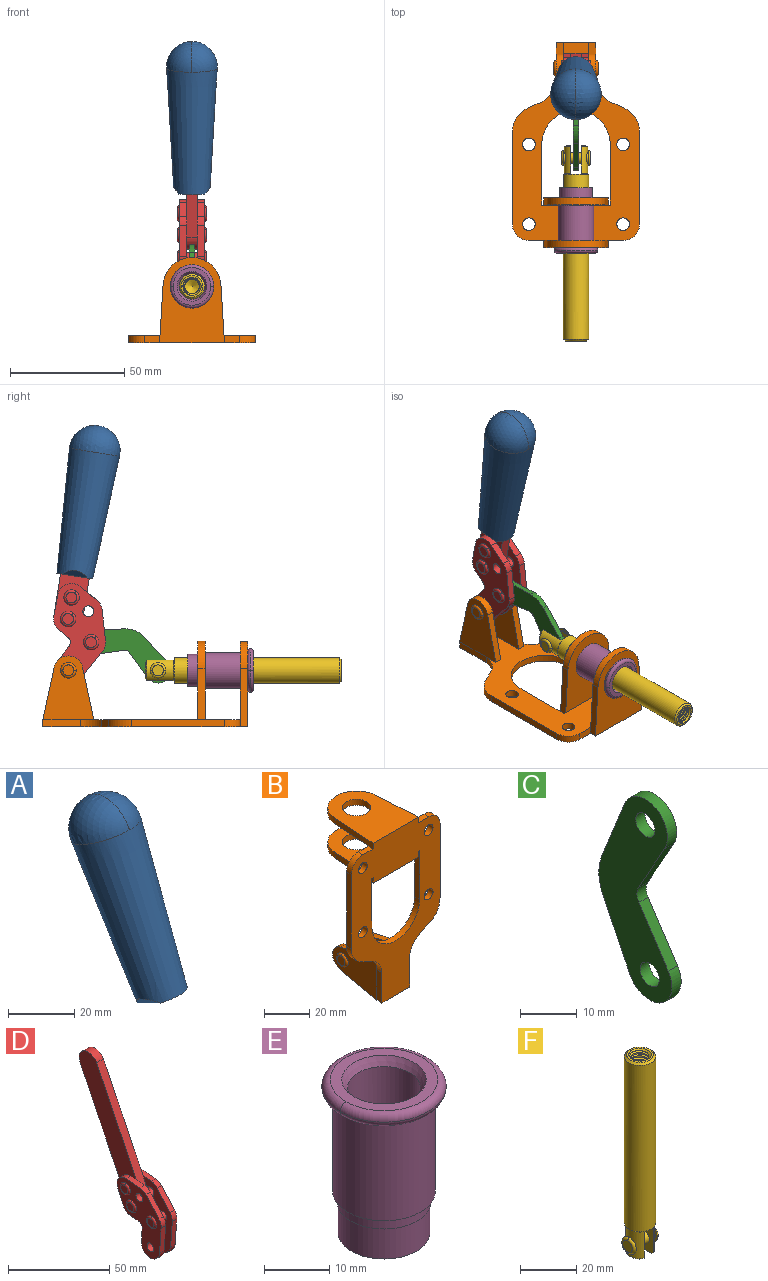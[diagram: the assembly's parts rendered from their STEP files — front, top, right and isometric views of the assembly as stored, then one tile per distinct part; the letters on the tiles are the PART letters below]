
ASSEMBLY  parts=6 mates=6
PART A: 11 faces, bbox 22.3x42.6x64.5 mm
  f0: sphere r=11.13mm, area 411.4mm2, adj f1,f8
  f1: cone r=11.11mm half-angle=3.3deg, axis (0,0.44,0.9), area 3251.8mm2, adj f0,f7,f8,f9,f10
  f2: cylinder r=6.16mm len=11.7mm, axis (1,0,0), area 89.5mm2, adj f3,f4,f5,f6
  f3: plane 60.23x36.75mm, normal (-1,0,0), area 763.6mm2, adj f2,f4,f6,f10
  f4: plane 51.37x25.05mm, normal (0,0.9,-0.44), area 264.2mm2, adj f2,f3,f5,f10
  f5: plane 60.23x36.75mm, normal (1,0,0), area 763.6mm2, adj f2,f4,f6,f10
  f6: plane 51.37x25.05mm, normal (0,-0.9,0.44), area 264.2mm2, adj f2,f3,f5,f10
  f7: plane 9.95x5.95mm, normal (0.71,-0.31,-0.64), area 25.8mm2, adj f1,f10
  f8: sphere r=11.13mm, area 411.4mm2, adj f0,f1
  f9: plane 9.95x5.95mm, normal (-0.71,-0.31,-0.64), area 25.8mm2, adj f1,f10
  f10: plane 14.27x11.38mm, normal (0,-0.44,-0.9), area 106.7mm2, adj f1,f3,f4,f5,f6,f7,f9
PART B: 55 faces, bbox 55.7x37.4x89.8 mm
  f0: torus R=2.41mm, axis (-1,0,0), area 15mm2, adj f11,f15,f25
  f1: torus R=2.41mm, axis (-1,0,0), area 15mm2, adj f10,f12,f22
  f2: cylinder r=2.78mm len=5.56mm, axis (0,-1,0), area 54.2mm2, adj f30,f54
  f3: cylinder r=14.99mm len=29.97mm, axis (0,-1,0), area 145.9mm2, adj f30,f49,f53,f54
  f4: cylinder r=2.78mm len=5.56mm, axis (0,-1,0), area 54.2mm2, adj f30,f54
  f5: cylinder r=2.78mm len=5.56mm, axis (0,-1,0), area 54.2mm2, adj f30,f54
  f6: cylinder r=2.78mm len=5.56mm, axis (0,-1,0), area 54.2mm2, adj f30,f54
  f7: cylinder r=6.35mm len=12.7mm, axis (0,0,1), area 123.6mm2, adj f27,f51
  f8: cylinder r=6.35mm len=12.7mm, axis (0,0,-1), area 124.7mm2, adj f21,f35
  f9: cylinder r=2.41mm len=11.18mm, axis (-1,0,0), area 169.4mm2, adj f16,f19
  f10: plane 4.83x4.83mm, normal (1,0,0), area 18.3mm2, adj f1,f12
  f11: plane 4.83x4.83mm, normal (-1,0,0), area 18.3mm2, adj f0,f15
  f12: torus R=2.41mm, axis (-1,0,0), area 15mm2, adj f1,f10,f22
  f13: cylinder r=6.35mm len=12.41mm, axis (1,0,0), area 53.4mm2, adj f18,f19,f22,f23
  f14: cylinder r=6.35mm len=12.41mm, axis (-1,0,0), area 53.4mm2, adj f16,f17,f24,f25
  f15: torus R=2.41mm, axis (-1,0,0), area 15mm2, adj f0,f11,f25
  f16: plane 27.86x22.35mm, normal (1,0,0), area 425.4mm2, adj f9,f14,f17,f24,f30
  f17: plane 22.86x4.97mm, normal (0,0.21,0.98), area 72.5mm2, adj f14,f16,f25,f30
  f18: plane 22.86x4.97mm, normal (0,0.21,0.98), area 72.5mm2, adj f13,f19,f22,f30
  f19: plane 27.86x22.35mm, normal (-1,0,0), area 425.4mm2, adj f9,f13,f18,f23,f30
  f20: cylinder r=12.7mm len=25.35mm, axis (0,0,-1), area 119.8mm2, adj f21,f34,f35,f36
  f21: plane 34.21x28.07mm, normal (0,0,-1), area 702.4mm2, adj f8,f20,f30,f34,f36
  f22: plane 27.96x22.45mm, normal (1,0,0), area 407.2mm2, adj f1,f12,f13,f18,f23,f30,f42,f43
  f23: plane 22.86x4.97mm, normal (0,0.21,-0.98), area 72.5mm2, adj f13,f19,f22,f44
  f24: plane 22.86x4.97mm, normal (0,0.21,-0.98), area 72.5mm2, adj f14,f16,f25,f44
  f25: plane 27.86x22.35mm, normal (-1,0,0), area 407.1mm2, adj f0,f14,f15,f17,f24,f30,f45,f46
  f26: plane 3.1x0.95mm, normal (0,0,-1), area 2.7mm2, adj f30,f49,f50,f54
  f27: plane 34.21x28.07mm, normal (0,0,1), area 702.4mm2, adj f7,f28,f30,f50,f52
  f28: cylinder r=12.7mm len=25.35mm, axis (0,0,1), area 118.8mm2, adj f27,f50,f51,f52
  f29: plane 3.1x0.95mm, normal (0,0,-1), area 2.7mm2, adj f30,f52,f53,f54
  f30: plane 86.54x55.63mm, normal (0,1,0), area 2362.9mm2, adj f2,f3,f4,f5,f6,f16,f17,f18
  f31: plane 40.56x3.1mm, normal (-1,0,0), area 125.7mm2, adj f30,f32,f48,f54
  f32: cylinder r=7.11mm len=7.11mm, axis (0,-1,0), area 34.6mm2, adj f30,f31,f33,f54
  f33: plane 6.67x3.1mm, normal (0,0,1), area 20.4mm2, adj f30,f32,f34,f54
  f34: plane 25.39x3.13mm, normal (-1,0.06,0), area 79.5mm2, adj f20,f21,f33,f35,f54
  f35: plane 37.31x28.45mm, normal (0,0,1), area 789.9mm2, adj f8,f20,f34,f36,f54
  f36: plane 25.39x3.13mm, normal (1,0.06,0), area 79.5mm2, adj f20,f21,f35,f37,f54
  f37: plane 6.67x3.1mm, normal (0,0,1), area 20.4mm2, adj f30,f36,f38,f54
  f38: cylinder r=7.11mm len=7.11mm, axis (0,-1,0), area 34.6mm2, adj f30,f37,f39,f54
  f39: plane 40.56x3.1mm, normal (1,0,0), area 125.7mm2, adj f30,f38,f40,f54
  f40: cylinder r=11.18mm len=10.16mm, axis (0,-1,0), area 39.5mm2, adj f30,f39,f41,f54
  f41: plane 6.09x3.1mm, normal (0.42,0,-0.91), area 20.8mm2, adj f30,f40,f42,f54
  f42: cylinder r=11.18mm len=9.41mm, axis (0,-1,0), area 37.2mm2, adj f22,f30,f41,f43,f54
  f43: plane 16.5x3.1mm, normal (1,0,0), area 51.1mm2, adj f22,f42,f44,f54
  f44: plane 17.37x3.1mm, normal (0,0,-1), area 53.8mm2, adj f23,f24,f30,f43,f45,f54
  f45: plane 16.5x3.1mm, normal (-1,0,0), area 51.1mm2, adj f25,f44,f46,f54
  f46: cylinder r=11.18mm len=9.41mm, axis (0,-1,0), area 37.2mm2, adj f25,f30,f45,f47,f54
  f47: plane 6.09x3.1mm, normal (-0.42,0,-0.91), area 20.8mm2, adj f30,f46,f48,f54
  f48: cylinder r=11.18mm len=10.16mm, axis (0,-1,0), area 39.5mm2, adj f30,f31,f47,f54
  f49: plane 26.54x3.1mm, normal (-1,0,0), area 82.3mm2, adj f3,f26,f30,f54
  f50: plane 25.39x3.1mm, normal (1,0.06,0), area 78.8mm2, adj f26,f27,f28,f51,f54
  f51: plane 37.31x28.45mm, normal (0,0,-1), area 789.9mm2, adj f7,f28,f50,f52,f54
  f52: plane 25.39x3.1mm, normal (-1,0.06,0), area 78.8mm2, adj f27,f28,f29,f51,f54
  f53: plane 26.54x3.1mm, normal (1,0,0), area 82.3mm2, adj f3,f29,f30,f54
  f54: plane 89.66x55.63mm, normal (0,-1,0), area 2678.5mm2, adj f2,f3,f4,f5,f6,f26,f29,f31
PART C: 12 faces, bbox 2.3x18.2x42.8 mm
  f0: cylinder r=2.4mm len=4.8mm, axis (1,0,0), area 34.9mm2, adj f4,f11
  f1: cylinder r=10.41mm len=8.47mm, axis (1,0,0), area 20.2mm2, adj f4,f9,f10,f11
  f2: cylinder r=3.05mm len=3.16mm, axis (1,0,0), area 7.7mm2, adj f4,f6,f7,f11
  f3: cylinder r=2.4mm len=4.8mm, axis (1,0,0), area 34.9mm2, adj f4,f11
  f4: plane 42.81x18.23mm, normal (-1,0,0), area 414.1mm2, adj f0,f1,f2,f3,f5,f6,f7,f8
  f5: cylinder r=5.54mm len=10.67mm, axis (1,0,0), area 41.8mm2, adj f4,f6,f10,f11
  f6: plane 11.66x6.53mm, normal (0,-0.87,-0.49), area 30.9mm2, adj f2,f4,f5,f11
  f7: plane 11.17x7.33mm, normal (0,-0.84,0.55), area 30.9mm2, adj f2,f4,f8,f11
  f8: cylinder r=5.54mm len=10.51mm, axis (1,0,0), area 41.8mm2, adj f4,f7,f9,f11
  f9: plane 13.67x6.67mm, normal (0,0.9,-0.44), area 35.1mm2, adj f1,f4,f8,f11
  f10: plane 14.1x5.7mm, normal (0,0.93,0.37), area 35.1mm2, adj f1,f4,f5,f11
  f11: plane 42.81x18.23mm, normal (1,0,0), area 414.1mm2, adj f0,f1,f2,f3,f5,f6,f7,f8
PART D: 59 faces, bbox 12.9x60.2x99.6 mm
  f0: torus R=2.39mm, axis (-1,0,0), area 14.9mm2, adj f20,f43,f51
  f1: torus R=2.39mm, axis (-1,0,0), area 14.9mm2, adj f19,f42,f51
  f2: torus R=2.39mm, axis (-1,0,0), area 14.9mm2, adj f18,f35,f51
  f3: torus R=2.39mm, axis (-1,0,0), area 14.9mm2, adj f14,f17,f23
  f4: torus R=2.39mm, axis (-1,0,0), area 14.9mm2, adj f13,f16,f23
  f5: torus R=2.39mm, axis (-1,0,0), area 14.9mm2, adj f12,f15,f23
  f6: cylinder r=2.39mm len=4.78mm, axis (1,0,0), area 46.5mm2, adj f48,f50,f51
  f7: cylinder r=2.39mm len=4.78mm, axis (1,0,0), area 46.5mm2, adj f50,f51
  f8: cylinder r=6.35mm len=12.68mm, axis (1,0,0), area 61.8mm2, adj f38,f39,f50,f51
  f9: cylinder r=2.39mm len=4.78mm, axis (-1,0,0), area 70.5mm2, adj f46,f50
  f10: cylinder r=2.39mm len=4.78mm, axis (-1,0,0), area 46.5mm2, adj f23,f45,f46
  f11: cylinder r=2.39mm len=4.78mm, axis (-1,0,0), area 46.5mm2, adj f23,f46
  f12: plane 4.78x4.78mm, normal (1,0,0), area 17.9mm2, adj f5,f15
  f13: plane 4.78x4.78mm, normal (1,0,0), area 17.9mm2, adj f4,f16
  f14: plane 4.78x4.78mm, normal (1,0,0), area 17.9mm2, adj f3,f17
  f15: torus R=2.39mm, axis (-1,0,0), area 14.9mm2, adj f5,f12,f23
  f16: torus R=2.39mm, axis (-1,0,0), area 14.9mm2, adj f4,f13,f23
  f17: torus R=2.39mm, axis (-1,0,0), area 14.9mm2, adj f3,f14,f23
  f18: plane 4.78x4.78mm, normal (-1,0,0), area 17.9mm2, adj f2,f35
  f19: plane 4.78x4.78mm, normal (-1,0,0), area 17.9mm2, adj f1,f42
  f20: plane 4.78x4.78mm, normal (-1,0,0), area 17.9mm2, adj f0,f43
  f21: plane 2.26x0.2mm, normal (1,0,0), area 0.2mm2, adj f31,f44
  f22: plane 2.26x0.2mm, normal (-1,0,0), area 0.2mm2, adj f41,f44
  f23: plane 39.37x30.77mm, normal (1,0,0), area 565.5mm2, adj f3,f4,f5,f10,f11,f15,f16,f17
  f24: cylinder r=6.1mm len=4.15mm, axis (-1,0,0), area 14.7mm2, adj f23,f25,f32,f46
  f25: plane 10.25x9.01mm, normal (0,-0.75,0.66), area 42.3mm2, adj f23,f24,f26,f46
  f26: cylinder r=6.35mm len=4.64mm, axis (-1,0,0), area 15.6mm2, adj f23,f25,f27,f46
  f27: plane 15.84x3.1mm, normal (0,-1,-0.07), area 49.2mm2, adj f23,f26,f28,f46
  f28: cylinder r=6.35mm len=12.68mm, axis (-1,0,0), area 61.8mm2, adj f23,f27,f29,f46
  f29: plane 8.11x3.1mm, normal (0,1,0.07), area 25.2mm2, adj f23,f28,f30,f46
  f30: cylinder r=3.05mm len=3.25mm, axis (-1,0,0), area 14.8mm2, adj f23,f29,f31,f46
  f31: plane 5.99x3.1mm, normal (0,0.07,-1), area 18.6mm2, adj f21,f23,f30,f44,f46
  f32: plane 9.5x3.1mm, normal (0,-0.07,1), area 29.5mm2, adj f23,f24,f33,f46,f47
  f33: cylinder r=6.1mm len=8.63mm, axis (-1,0,0), area 39.1mm2, adj f23,f32,f34,f47
  f34: plane 8.65x3.96mm, normal (0,0.91,-0.42), area 29.5mm2, adj f23,f33,f44,f47
  f35: torus R=2.39mm, axis (-1,0,0), area 14.9mm2, adj f2,f18,f51
  f36: plane 10.25x9.01mm, normal (0,-0.75,0.66), area 42.3mm2, adj f37,f49,f50,f51
  f37: cylinder r=6.35mm len=4.64mm, axis (1,0,0), area 15.6mm2, adj f36,f38,f50,f51
  f38: plane 15.84x3.1mm, normal (0,-1,-0.07), area 49.2mm2, adj f8,f37,f50,f51
  f39: plane 8.11x3.1mm, normal (0,1,0.07), area 25.2mm2, adj f8,f40,f50,f51
  f40: cylinder r=3.05mm len=3.25mm, axis (1,0,0), area 14.8mm2, adj f39,f41,f50,f51
  f41: plane 5.99x3.1mm, normal (0,0.07,-1), area 18.6mm2, adj f22,f40,f44,f50,f51
  f42: torus R=2.39mm, axis (-1,0,0), area 14.9mm2, adj f1,f19,f51
  f43: torus R=2.39mm, axis (-1,0,0), area 14.9mm2, adj f0,f20,f51
  f44: cylinder r=6.35mm len=12.12mm, axis (-1,0,0), area 128.9mm2, adj f21,f22,f23,f31,f34,f41,f46,f47
  f45: plane 2.65x1.35mm, normal (1,0,0), area 1mm2, adj f10,f55
  f46: plane 39.08x20.42mm, normal (-1,0,0), area 412.5mm2, adj f9,f10,f11,f24,f25,f26,f27,f28
  f47: plane 77.62x39.82mm, normal (1,0,0), area 850mm2, adj f32,f33,f34,f44,f53,f54,f55
  f48: plane 2.65x1.35mm, normal (-1,0,0), area 1mm2, adj f6,f55
  f49: cylinder r=6.1mm len=4.15mm, axis (1,0,0), area 14.7mm2, adj f36,f50,f51,f56
  f50: plane 39.08x20.42mm, normal (1,0,0), area 412.5mm2, adj f6,f7,f8,f9,f36,f37,f38,f39
  f51: plane 39.37x30.77mm, normal (-1,0,0), area 565.5mm2, adj f0,f1,f2,f6,f7,f8,f35,f36
  f52: plane 8.65x3.96mm, normal (0,0.91,-0.42), area 29.5mm2, adj f44,f51,f57,f58
  f53: plane 68.49x33.4mm, normal (0,0.9,-0.44), area 358.1mm2, adj f44,f47,f54,f58
  f54: cylinder r=6.35mm len=12.06mm, axis (1,0,0), area 93.7mm2, adj f47,f53,f55,f58
  f55: plane 68.49x33.4mm, normal (0,-0.9,0.44), area 358.1mm2, adj f44,f45,f46,f47,f48,f50,f54,f58
  f56: plane 9.5x3.1mm, normal (0,-0.07,1), area 29.5mm2, adj f49,f50,f51,f57,f58
  f57: cylinder r=6.1mm len=8.63mm, axis (1,0,0), area 39.1mm2, adj f51,f52,f56,f58
  f58: plane 77.62x39.82mm, normal (-1,0,0), area 850mm2, adj f44,f52,f53,f54,f55,f56,f57
PART E: 15 faces, bbox 20.6x20.6x28.7 mm
  f0: torus R=8.26mm, axis (0,0,1), area 56.8mm2, adj f1,f10,f12
  f1: torus R=8.26mm, axis (0,0,1), area 56.8mm2, adj f0,f6,f13
  f2: cylinder r=5.59mm len=25.91mm, axis (0,0,1), area 909.6mm2, adj f3,f4
  f3: cone r=6.86mm half-angle=45deg, axis (0,0,-1), area 70.2mm2, adj f2,f14
  f4: cone r=6.47mm half-angle=30deg, axis (0,0,1), area 66.7mm2, adj f2,f13
  f5: cylinder r=7.04mm len=14.07mm, axis (0,0,1), area 252.6mm2, adj f11,f14
  f6: torus R=8.26mm, axis (0,0,1), area 56.8mm2, adj f1,f12,f13
  f7: cylinder r=7.16mm len=14.33mm, axis (0,0,1), area 91.5mm2, adj f9,f11
  f8: cylinder r=7.86mm len=18.42mm, axis (0,0,1), area 909.6mm2, adj f9,f10
  f9: plane 15.72x15.72mm, normal (0,0,-1), area 33mm2, adj f7,f8
  f10: plane 16.51x16.51mm, normal (0,0,-1), area 19.9mm2, adj f0,f8,f12
  f11: plane 14.33x14.33mm, normal (0,0,-1), area 5.7mm2, adj f5,f7
  f12: torus R=8.26mm, axis (0,0,1), area 56.8mm2, adj f0,f6,f10
  f13: plane 16.51x16.51mm, normal (0,0,1), area 82.7mm2, adj f1,f4,f6
  f14: plane 14.07x14.07mm, normal (0,0,-1), area 7.8mm2, adj f3,f5
PART F: 48 faces, bbox 12.6x11.1x86.1 mm
  f0: torus R=2.41mm, axis (-1,0,0), area 15mm2, adj f30,f32,f34
  f1: torus R=2.41mm, axis (-1,0,0), area 15mm2, adj f29,f31,f33
  f2: cylinder r=5.54mm len=72.39mm, axis (0,0,1), area 2518.5mm2, adj f3,f4,f42,f43
  f3: cone r=5.54mm half-angle=45deg, axis (0,0,1), area 7.6mm2, adj f2,f5,f41
  f4: cone r=5.54mm half-angle=45deg, axis (0,0,-1), area 34.9mm2, adj f2,f39
  f5: cylinder r=5.08mm len=11.48mm, axis (0,0,1), area 108.3mm2, adj f3,f7,f8,f41
  f6: cylinder r=2.41mm len=4.83mm, axis (-1,0,0), area 71.2mm2, adj f40,f41
  f7: cylinder r=2.41mm len=4.83mm, axis (-1,0,0), area 7.6mm2, adj f5,f34
  f8: cone r=5.08mm half-angle=45deg, axis (0,0,1), area 10.6mm2, adj f5,f37,f41
  f9: cone r=3.98mm half-angle=45deg, axis (0,0,1), area 17.6mm2, adj f27,f39,f45,f46,f47
  f10: cylinder r=2.41mm len=4.83mm, axis (-1,0,0), area 7.6mm2, adj f33,f38
  f11: cylinder r=3.2mm len=6.4mm, axis (0,0,1), area 78.4mm2, adj f12,f28,f44,f45,f47
  f12: cylinder r=3.2mm len=6.4mm, axis (0,0,1), area 10.5mm2, adj f11,f13,f45,f47
  f13: cylinder r=3.2mm len=6.4mm, axis (0,0,1), area 10.5mm2, adj f12,f14,f45,f47
  f14: cylinder r=3.2mm len=6.4mm, axis (0,0,1), area 10.5mm2, adj f13,f15,f45,f47
  f15: cylinder r=3.2mm len=6.4mm, axis (0,0,1), area 10.5mm2, adj f14,f16,f45,f47
  f16: cylinder r=3.2mm len=6.4mm, axis (0,0,1), area 10.5mm2, adj f15,f17,f45,f47
  f17: cylinder r=3.2mm len=6.4mm, axis (0,0,1), area 10.5mm2, adj f16,f18,f45,f47
  f18: cylinder r=3.2mm len=6.4mm, axis (0,0,1), area 10.5mm2, adj f17,f19,f45,f47
  f19: cylinder r=3.2mm len=6.4mm, axis (0,0,1), area 10.5mm2, adj f18,f20,f45,f47
  f20: cylinder r=3.2mm len=6.4mm, axis (0,0,1), area 10.5mm2, adj f19,f21,f45,f47
  f21: cylinder r=3.2mm len=6.4mm, axis (0,0,1), area 10.5mm2, adj f20,f22,f45,f47
  f22: cylinder r=3.2mm len=6.4mm, axis (0,0,1), area 10.5mm2, adj f21,f23,f45,f47
  f23: cylinder r=3.2mm len=6.4mm, axis (0,0,1), area 10.5mm2, adj f22,f24,f45,f47
  f24: cylinder r=3.2mm len=6.4mm, axis (0,0,1), area 10.5mm2, adj f23,f25,f45,f47
  f25: cylinder r=3.2mm len=6.4mm, axis (0,0,1), area 10.5mm2, adj f24,f26,f45,f47
  f26: cylinder r=3.2mm len=6.4mm, axis (0,0,1), area 10.5mm2, adj f25,f27,f45,f47
  f27: cylinder r=3.2mm len=6.4mm, axis (0,0,1), area 7.4mm2, adj f9,f26,f45,f47
  f28: cone r=3.2mm half-angle=60deg, axis (0,0,1), area 37.2mm2, adj f11
  f29: plane 4.83x4.83mm, normal (-1,0,0), area 18.3mm2, adj f1,f31
  f30: plane 4.83x4.83mm, normal (1,0,0), area 18.3mm2, adj f0,f32
  f31: torus R=2.41mm, axis (-1,0,0), area 15mm2, adj f1,f29,f33
  f32: torus R=2.41mm, axis (-1,0,0), area 15mm2, adj f0,f30,f34
  f33: plane 6.83x6.83mm, normal (1,0,0), area 18.3mm2, adj f1,f10,f31
  f34: plane 6.83x6.83mm, normal (-1,0,0), area 18.3mm2, adj f0,f7,f32
  f35: cone r=5.08mm half-angle=45deg, axis (0,0,1), area 10.6mm2, adj f36,f38,f40
  f36: plane 7.25x1.97mm, normal (0,0,-1), area 10mm2, adj f35,f40
  f37: plane 7.25x1.97mm, normal (0,0,-1), area 10mm2, adj f8,f41
  f38: cylinder r=5.08mm len=11.48mm, axis (0,0,1), area 108.3mm2, adj f10,f35,f40,f42
  f39: plane 9.55x9.55mm, normal (0,0,1), area 22mm2, adj f4,f9
  f40: plane 12.76x10.09mm, normal (1,0,0), area 95.7mm2, adj f6,f35,f36,f38,f42,f43
  f41: plane 12.76x10.09mm, normal (-1,0,0), area 95.7mm2, adj f3,f5,f6,f8,f37,f43
  f42: cone r=5.54mm half-angle=45deg, axis (0,0,1), area 7.6mm2, adj f2,f38,f40
  f43: plane 11.07x4.7mm, normal (0,0,-1), area 50.4mm2, adj f2,f40,f41
  f44: plane 0.89x0.62mm, normal (-1,0,0), area 0.3mm2, adj f11,f45,f46,f47
  f45: bspline ~24.8x7.63mm, area 266.6mm2, adj f9,f11,f12,f13,f14,f15,f16,f17
  f46: bspline ~24.87x7.63mm, area 73.6mm2, adj f9,f44,f45,f47
  f47: bspline ~24.98x7.63mm, area 272.5mm2, adj f9,f11,f12,f13,f14,f15,f16,f17
PLACE A rot(axis=(1,0,0),35deg) t=(-0.04,2.95,36.78)mm
PLACE B rot(axis=(1,0,0),90deg) t=(0,9.43,0)mm fixed
PLACE C rot(axis=(0,-0.57,-0.82),180deg) t=(0,25.84,8.44)mm
PLACE D rot(axis=(1,0,0),35deg) t=(0,2.95,36.78)mm
PLACE E rot(axis=(1,0,0),90deg) t=(0,9.43,0)mm
PLACE F rot(axis=(1,0,0),90deg) t=(0,17.75,0)mm
MATE revolute C.f5 <-> D.f4  axis (-1,0,0) through (0,31.53,36.95)mm
MATE revolute C.f3 <-> F.f6  axis (-1,0,0) through (0,2.28,24.61)mm
MATE fastened B.f7 <-> E.f2  axis (0,-1,0) through (0,-36.96,24.61)mm
MATE fastened D.f54 <-> A.f2  axis (-1,0,0) through (-2.35,29.73,122.4)mm
MATE revolute B.f0 <-> D.f7  axis (-1,0,0) through (0,41.52,24.61)mm
MATE slider B.f7 <-> F.f2  axis (0,-1,0) through (0,-36.96,24.61)mm
